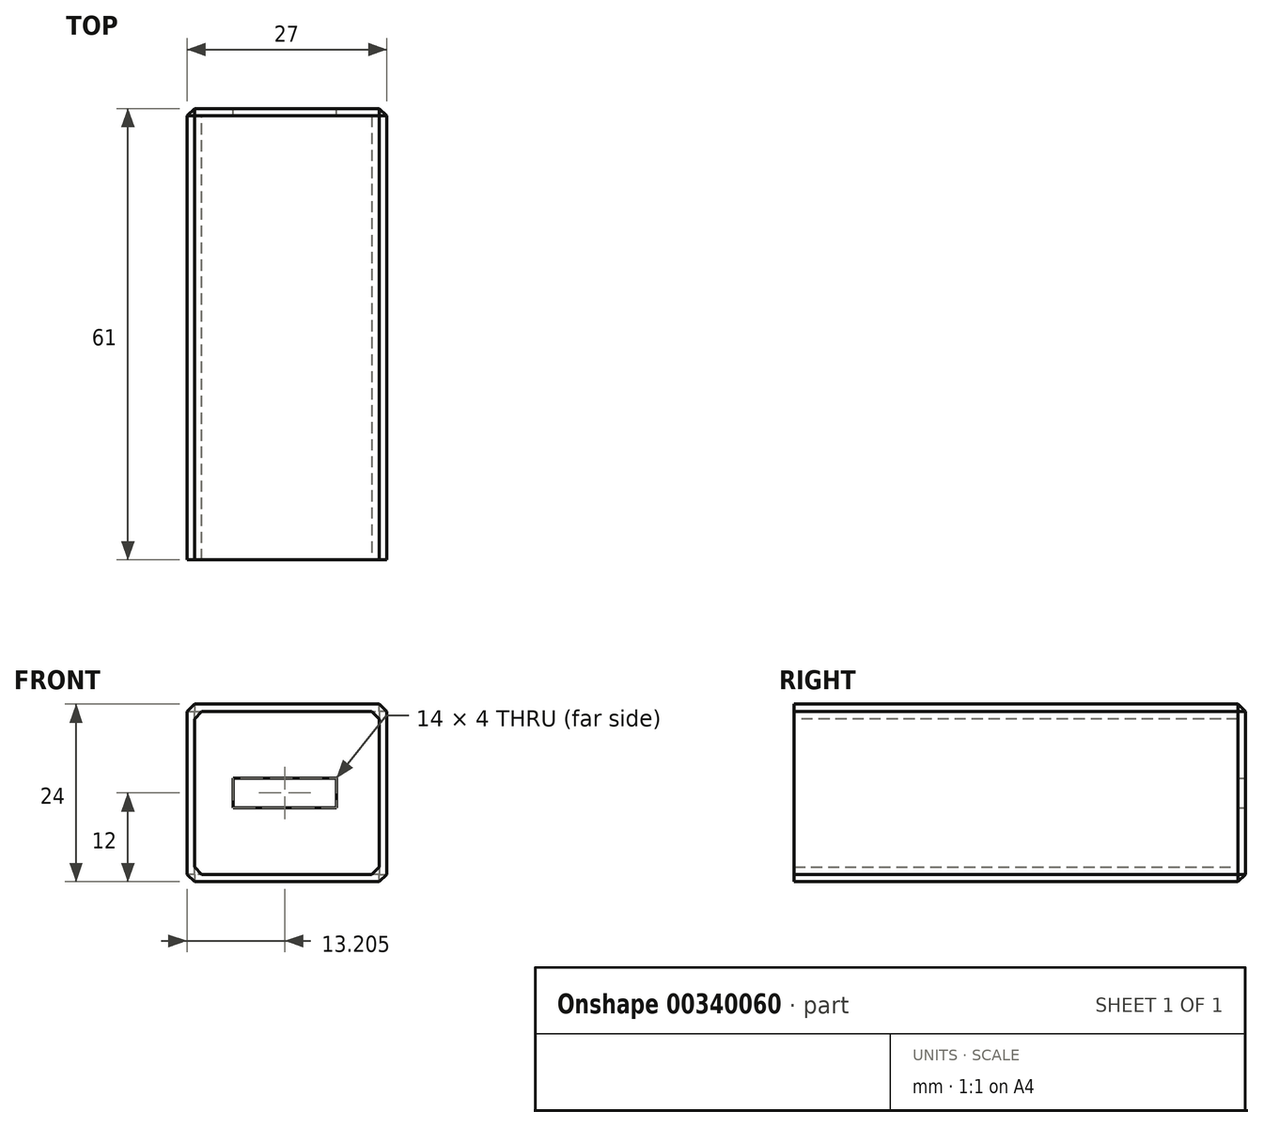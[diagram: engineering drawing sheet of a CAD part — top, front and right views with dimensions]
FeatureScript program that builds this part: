
annotation { "Feature Type Name" : "Feature", "Feature Type Description" : "" }
export const myFeature = defineFeature(function(context is Context, id is Id, definition is map)
    precondition{}
    {
        {
            var Q0;
            Q0=qCreatedBy(makeId("Front.planeOp"),FACE);
            var sketch = newSketch(context, id + "F0", { "sketchPlane" : qUnion([Q0])});
            skLineSegment(sketch, "E0.bottom", {"start": v(0, 0) * mm, "end": v(25, 0) * mm});
            skLineSegment(sketch, "E0.top", {"start": v(0, -22) * mm, "end": v(25, -22) * mm});
            skLineSegment(sketch, "E0.left", {"start": v(0, 0) * mm, "end": v(0, -22) * mm});
            skLineSegment(sketch, "E0.right", {"start": v(25, 0) * mm, "end": v(25, -22) * mm});
            skLineSegment(sketch, "E1", {"start": v(-1, 1) * mm, "end": v(-1, -23) * mm});
            skLineSegment(sketch, "E2", {"start": v(-1, 1) * mm, "end": v(26, 1) * mm});
            skLineSegment(sketch, "E3", {"start": v(26, 1) * mm, "end": v(26, -23) * mm});
            skLineSegment(sketch, "E4", {"start": v(26, -23) * mm, "end": v(-1, -23) * mm});
            skLineSegment(sketch, "E5", {"start": v(12.5, 0) * mm, "end": v(12.5, -22) * mm, "construction": true});
            skSolve(sketch);
        }
        {
            var Q0;
            Q0=makeQuery(id+"F0.imprint","IMPRINT",FACE,{"disambiguationData":[TD([[makeQuery(id+"F0.imprint","IMPRINT",EDGE,{"derivedFrom":sQuery(id+"F0.wireOp",EDGE,"E0.bottom")}),1.0]])]});
            extrude(context, id + "F1", {"entities" : qUnion([Q0]), "depth" : 60 * mm});
        }
        {
            var Q0;
            Q0=makeQuery(id+"F0.imprint","IMPRINT",FACE,{"disambiguationData":[TD([[makeQuery(id+"F0.imprint","IMPRINT",EDGE,{"derivedFrom":sQuery(id+"F0.wireOp",EDGE,"E0.bottom")}),-1.0]])]});
            var Q1;
            Q1=makeQuery(id+"F0.imprint","IMPRINT",FACE,{"disambiguationData":[TD([[makeQuery(id+"F0.imprint","IMPRINT",EDGE,{"derivedFrom":sQuery(id+"F0.wireOp",EDGE,"E0.bottom")}),1.0]])]});
            extrude(context, id + "F2", {"entities" : qUnion([Q0, Q1]), "operationType" : NewBodyOperationType.ADD, "oppositeDirection" : true, "depth" : 1 * mm});
        }
        {
            var Q0;
            Q0=makeQuery(id+"F1.opExtrude","SWEPT_EDGE",EDGE,{"disambiguationData":[OSD([sQuery(id+"F0.wireOp",EDGE,"E0.bottom"),sQuery(id+"F0.wireOp",EDGE,"E0.left")])]});
            var Q1;
            Q1=makeQuery(id+"F1.opExtrude","CAP_EDGE",EDGE,{"disambiguationData":[OSD([sQuery(id+"F0.wireOp",EDGE,"E0.bottom")])],"isStart":true});
            var Q2;
            Q2=makeQuery(id+"F1.opExtrude","CAP_EDGE",EDGE,{"disambiguationData":[OSD([sQuery(id+"F0.wireOp",EDGE,"E0.left")])],"isStart":true});
            var Q3;
            Q3=makeQuery(id+"F1.opExtrude","SWEPT_EDGE",EDGE,{"disambiguationData":[OSD([sQuery(id+"F0.wireOp",EDGE,"E0.top"),sQuery(id+"F0.wireOp",EDGE,"E0.left")])]});
            var Q4;
            Q4=makeQuery(id+"F1.opExtrude","CAP_EDGE",EDGE,{"disambiguationData":[OSD([sQuery(id+"F0.wireOp",EDGE,"E0.top")])],"isStart":true});
            var Q5;
            Q5=makeQuery(id+"F1.opExtrude","SWEPT_EDGE",EDGE,{"disambiguationData":[OSD([sQuery(id+"F0.wireOp",EDGE,"E0.top"),sQuery(id+"F0.wireOp",EDGE,"E0.right")])]});
            var Q6;
            Q6=makeQuery(id+"F1.opExtrude","CAP_EDGE",EDGE,{"disambiguationData":[OSD([sQuery(id+"F0.wireOp",EDGE,"E0.right")])],"isStart":true});
            var Q7;
            Q7=makeQuery(id+"F1.opExtrude","SWEPT_EDGE",EDGE,{"disambiguationData":[OSD([sQuery(id+"F0.wireOp",EDGE,"E0.bottom"),sQuery(id+"F0.wireOp",EDGE,"E0.right")])]});
            var Q8;
            {var subQ0=sQuery(id+"F0.wireOp",EDGE,"E2");var subQ1=sQuery(id+"F0.wireOp",EDGE,"E1");Q8=makeQuery(id+"F2.boolean.opBoolean","MERGE",EDGE,{"derivedFrom":[makeQuery(id+"F1.opExtrude","SWEPT_EDGE",EDGE,{"disambiguationData":[OSD([subQ1,subQ0])]}),makeQuery(id+"F2.opExtrude","SWEPT_EDGE",EDGE,{"disambiguationData":[OSD([subQ1,subQ0])]})]});}
            var Q9;
            {var subQ0=sQuery(id+"F0.wireOp",EDGE,"E4");var subQ1=sQuery(id+"F0.wireOp",EDGE,"E1");Q9=makeQuery(id+"F2.boolean.opBoolean","MERGE",EDGE,{"derivedFrom":[makeQuery(id+"F1.opExtrude","SWEPT_EDGE",EDGE,{"disambiguationData":[OSD([subQ1,subQ0])]}),makeQuery(id+"F2.opExtrude","SWEPT_EDGE",EDGE,{"disambiguationData":[OSD([subQ1,subQ0])]})]});}
            var Q10;
            Q10=makeQuery(id+"F2.opExtrude","CAP_EDGE",EDGE,{"disambiguationData":[OSD([sQuery(id+"F0.wireOp",EDGE,"E1")])],"isStart":false});
            var Q11;
            {var subQ0=sQuery(id+"F0.wireOp",EDGE,"E4");var subQ1=sQuery(id+"F0.wireOp",EDGE,"E3");Q11=makeQuery(id+"F2.boolean.opBoolean","MERGE",EDGE,{"derivedFrom":[makeQuery(id+"F1.opExtrude","SWEPT_EDGE",EDGE,{"disambiguationData":[OSD([subQ1,subQ0])]}),makeQuery(id+"F2.opExtrude","SWEPT_EDGE",EDGE,{"disambiguationData":[OSD([subQ1,subQ0])]})]});}
            var Q12;
            {var subQ0=sQuery(id+"F0.wireOp",EDGE,"E3");var subQ1=sQuery(id+"F0.wireOp",EDGE,"E2");Q12=makeQuery(id+"F2.boolean.opBoolean","MERGE",EDGE,{"derivedFrom":[makeQuery(id+"F1.opExtrude","SWEPT_EDGE",EDGE,{"disambiguationData":[OSD([subQ1,subQ0])]}),makeQuery(id+"F2.opExtrude","SWEPT_EDGE",EDGE,{"disambiguationData":[OSD([subQ1,subQ0])]})]});}
            var Q13;
            Q13=makeQuery(id+"F2.opExtrude","CAP_EDGE",EDGE,{"disambiguationData":[OSD([sQuery(id+"F0.wireOp",EDGE,"E4")])],"isStart":false});
            var Q14;
            Q14=makeQuery(id+"F2.opExtrude","CAP_EDGE",EDGE,{"disambiguationData":[OSD([sQuery(id+"F0.wireOp",EDGE,"E3")])],"isStart":false});
            var Q15;
            Q15=makeQuery(id+"F2.opExtrude","CAP_EDGE",EDGE,{"disambiguationData":[OSD([sQuery(id+"F0.wireOp",EDGE,"E2")])],"isStart":false});
            chamfer(context, id + "F3", {"entities" : qUnion([Q0, Q1, Q2, Q3, Q4, Q5, Q6, Q7, Q8, Q9, Q10, Q11, Q12, Q13, Q14, Q15]), "width" : 1 * mm, "tangentPropagation" : true});
        }
        {
            var Q0;
            Q0=makeQuery(id+"F2.opExtrude","CAP_FACE",FACE,{"disambiguationData":[OSD([sQuery(id+"F0.wireOp",EDGE,"E1"),sQuery(id+"F0.wireOp",EDGE,"E2"),sQuery(id+"F0.wireOp",EDGE,"E3"),sQuery(id+"F0.wireOp",EDGE,"E4")])],"isStart":false});
            var sketch = newSketch(context, id + "F4", { "sketchPlane" : qUnion([Q0])});
            skLineSegment(sketch, "E6", {"start": v(-25, -11) * mm, "end": v(0, -11) * mm, "construction": true});
            skLineSegment(sketch, "E7", {"start": v(-12.5, -22) * mm, "end": v(-12.5, 0) * mm, "construction": true});
            skLineSegment(sketch, "E8.bottom", {"start": v(-19.2, -13) * mm, "end": v(-5.2, -13) * mm});
            skLineSegment(sketch, "E8.top", {"start": v(-19.2, -9) * mm, "end": v(-5.2, -9) * mm});
            skLineSegment(sketch, "E8.left", {"start": v(-19.2, -13) * mm, "end": v(-19.2, -9) * mm});
            skLineSegment(sketch, "E8.right", {"start": v(-5.2, -13) * mm, "end": v(-5.2, -9) * mm});
            skLineSegment(sketch, "E9", {"start": v(-19.2, -9) * mm, "end": v(-19.2, -11) * mm});
            skLineSegment(sketch, "E10", {"start": v(-19.2, -11) * mm, "end": v(-5.2, -11) * mm, "construction": true});
            skSolve(sketch);
        }
        {
            var Q0;
            Q0 = qSketchRegion(id + "F4", true);
            extrude(context, id + "F5", {"entities" : qUnion([Q0]), "operationType" : NewBodyOperationType.REMOVE, "oppositeDirection" : true, "depth" : 25 * mm});
        }
    });
